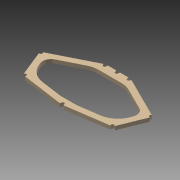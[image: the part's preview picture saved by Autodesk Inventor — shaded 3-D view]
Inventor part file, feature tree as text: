
AUTODESK INVENTOR PART (.ipt)
format: ipt  version: 2015 (Build 190159000, 159)  size: 196,608 bytes
history: native  units: mm
features: fillet x12, hole x5, extrude x2, sketch x2, mirror x1
ambient origin geometry x8: Origin, YZ Plane, XZ Plane, XY Plane, X Axis, Y Axis, Z Axis, Center Point
bodies: Solid4 (feature_tree)
feature tree (22):
  extrude  "Extrusion4"  Depth=279.1968mm
  hole  "Hole2"  [1 undecoded]
  hole  "Hole3"  [1 undecoded]
  hole  "Hole4"  [1 undecoded]
  hole  "Hole5"  [1 undecoded]
  hole  "Hole6"  [1 undecoded]
  fillet  "Fillet6"  Radius=18.0mm
  fillet  "Fillet7"  Radius=10.0mm
  fillet  "Fillet8"  Radius=5.0mm
  fillet  "Fillet9"  Radius=3.0mm
  fillet  "Fillet10"  Radius=3.0mm
  fillet  "Fillet11"  Radius=1.0mm
  fillet  "Fillet12"  Radius=1.0mm
  fillet  "Fillet13"  Radius=1.0mm
  extrude  "Extrusion5"  Depth=1.0mm
  fillet  "Fillet14"  Radius=3.5mm
  fillet  "Fillet15"  Radius=28.0mm
  fillet  "Fillet16"  Radius=28.0mm
  fillet  "Fillet17"  Radius=28.0mm
  mirror  "Mirror3"
  sketch  "Sketch1"  dims[d9=279.1968mm d11=275.5392mm]
  sketch  "Sketch4"  dims[d15=172.212mm d20=219.456mm d22=32.9184mm d39=60.96mm d41=0.0mm d42=1.2192mm d98=18.0mm d99=0.0mm d140=10.0mm d141=10.0mm d102=15.0mm d103=6.0mm d104=3.023mm d105=2.0mm d106=14.3117mm d107=8.0mm d108=20.594885mm d161=10.0mm d162=10.0mm d111=15.0mm d112=6.0mm d113=3.023mm d114=2.0mm d115=14.3117mm d116=8.0mm d117=20.594885mm d157=10.0mm d158=10.0mm d124=15.0mm d125=6.0mm d126=3.023mm d127=2.0mm d128=14.3117mm d129=8.0mm d130=20.594885mm d159=10.0mm d160=10.0mm d133=15.0mm d134=6.0mm d135=3.023mm d136=2.0mm d137=14.3117mm d138=8.0mm d139=20.594885mm d144=10.0mm d145=10.0mm d150=15.0mm d151=6.0mm d152=4.0mm d153=2.0mm d154=90.0deg d155=8.0mm d156=20.594885mm d163=5.0mm d164=3.0mm d165=3.0mm d166=1.0mm d167=1.0mm d168=1.0mm d169=1.0mm d170=3.5mm d171=28.0mm d172=28.0mm d173=28.0mm d174=40.0mm d175=80.0mm d176=10.0mm d177=0.0mm d178=40.0mm d179=100.0mm d180=100.0mm d181=100.0mm]
note: 5 required parameter values undecoded (feature->parameter linkage not recoverable at this tier; creation-order binding heuristic only, values carry confidence <= 0.55)
